# Revit family: R 15 (a)
name_source: partatom
category: Equipement spécialisé
revit_build: Autodesk Revit LT 2015 (Build: 20140606_1530(x64)
units: mm (PartAtom-declared; Revit-internal decimal feet)

## types (5) — shared parameters
Apparent Power = 0 VA
Depth = 643 mm  [stored 2.10958 ft]
Description = CUTTERS VERTICAUX
Electrique connexion = 125 mm
Fabricant = ROBOT COUPE
Height = 678 mm
Phase = 3
UP Depth = 757 mm
UP Height = 970 mm
URL = www.robot-coupe.com
Width = 437 mm
water = Connector
zero-valued in all types: Cold water supply, Cold water supply height, Used water, Waste water height

## per-type parameters (varying)
| type | Amps | Cycle | HP | Modèle | Speeds (Rpm) | Volts | Watts | Weight |
| R 15   220/60/3 | 6.5 & 11 A | 60 Hz |  | R 15 | 1500 & 3000 | 220 V | 3000 W | 58.7 kg |
| R 15   380/60/3 | 7 & 12 A | 60 Hz |  | R 15 | 1500 & 3000 | 380 V | 3000 W | 58.7 kg |
| R 15   230/50/3 | 7 & 13 A | 50 Hz |  | R 15 | 1500 & 3000 | 230 V | 3000 W | 58.7 kg |
| R 15 USA    208-240/60/3 | 7 & 13 A | 60 Hz | 4.5 | R 15 USA | 1800 & 3600 | 208 V | 0 W | 132 lbs |
| R 15   400/50/3 | 6.5 & 12 A | 50 Hz |  | R 15 | 1500 & 3000 | 400 V | 3000 W | 58.7 kg |

note: [stored X ft] marks values corroborated as IEEE doubles in the binary element streams (Revit-internal decimal feet)

## geometry (parser evidence)
native form markers: Blend x100, Sweep x4
no freeform markers — native parametric forms only
